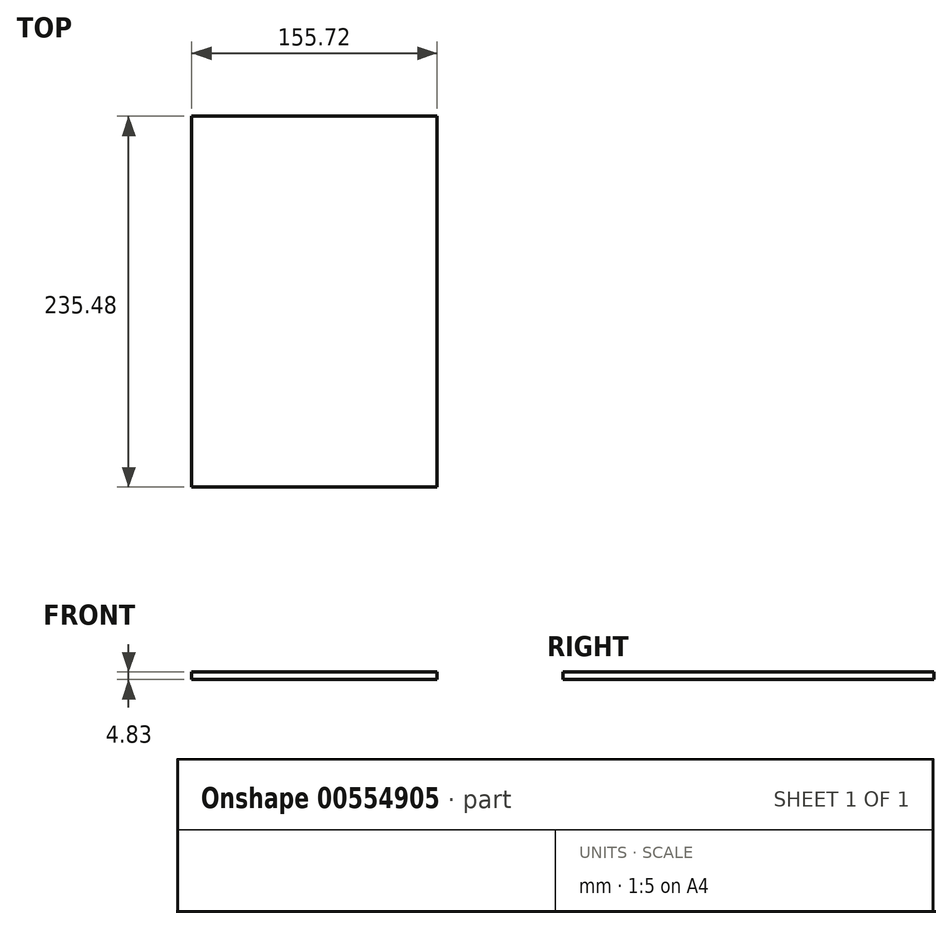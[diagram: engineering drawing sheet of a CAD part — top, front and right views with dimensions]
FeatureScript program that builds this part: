
annotation { "Feature Type Name" : "Feature", "Feature Type Description" : "" }
export const myFeature = defineFeature(function(context is Context, id is Id, definition is map)
    precondition{}
    {
        {
            var Q0;
            Q0=qCreatedBy(makeId("Top.planeOp"),FACE);
            var sketch = newSketch(context, id + "F0", { "sketchPlane" : qUnion([Q0])});
            skLineSegment(sketch, "E0.bottom", {"start": v(-78.8, 121.84) * mm, "end": v(76.93, 121.84) * mm});
            skLineSegment(sketch, "E0.top", {"start": v(-78.8, -113.64) * mm, "end": v(76.93, -113.64) * mm});
            skLineSegment(sketch, "E0.left", {"start": v(-78.8, 121.84) * mm, "end": v(-78.8, -113.64) * mm});
            skLineSegment(sketch, "E0.right", {"start": v(76.93, 121.84) * mm, "end": v(76.93, -113.64) * mm});
            skSolve(sketch);
        }
        {
            var Q0;
            Q0 = qSketchRegion(id + "F0", true);
            extrude(context, id + "F1", {"entities" : qUnion([Q0]), "depth" : 4.83 * mm, "offsetDistance" : 25.4 * mm});
        }
    });
